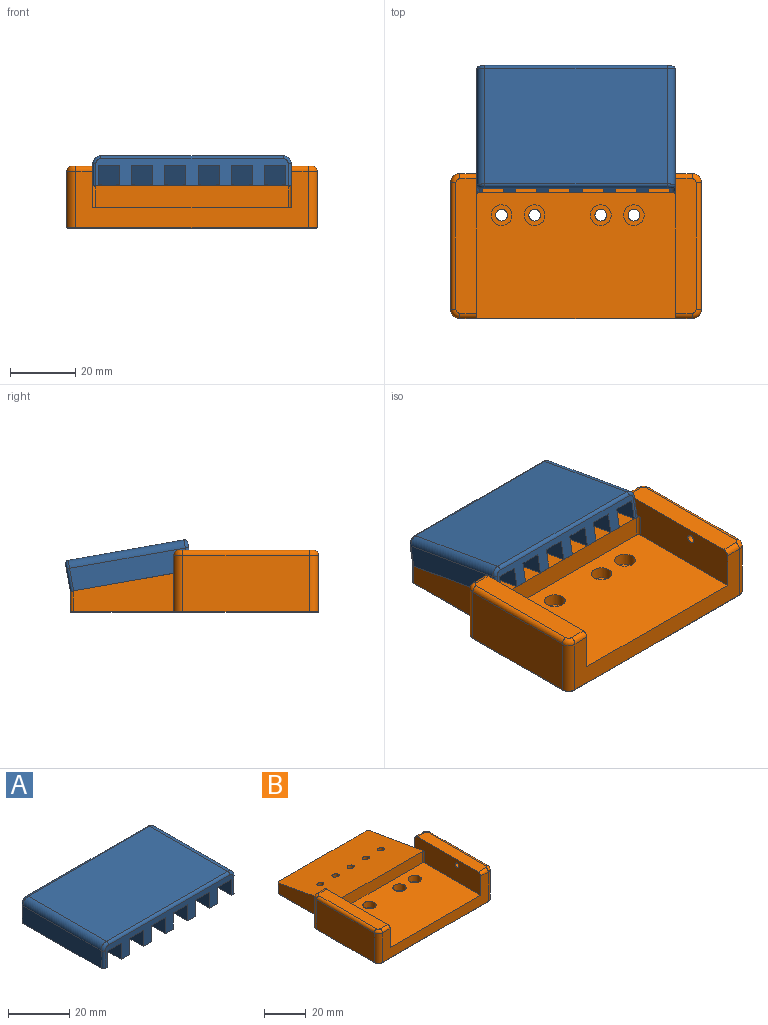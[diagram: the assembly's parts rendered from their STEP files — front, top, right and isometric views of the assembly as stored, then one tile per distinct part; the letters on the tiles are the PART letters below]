
ASSEMBLY  parts=2 mates=1
PART A: 58 faces, bbox 61.4x38.1x10.2 mm
  f0: plane 59.01x8.53mm, normal (0,-1,0), area 250.4mm2, adj f8,f9,f10,f11,f12,f13,f14,f17
  f1: plane 59.01x8.53mm, normal (0,1,0), area 439.9mm2, adj f23,f40,f41,f42,f43,f44,f45,f46
  f2: cylinder r=3.24mm len=6.48mm, axis (0,0,-1), area 55.1mm2, adj f13,f14,f23,f29,f45
  f3: cylinder r=3.24mm len=6.48mm, axis (0,0,-1), area 55.1mm2, adj f12,f21,f23,f24,f44
  f4: cylinder r=3.24mm len=6.48mm, axis (0,0,-1), area 55.1mm2, adj f11,f18,f23,f27,f43
  f5: cylinder r=3.24mm len=6.48mm, axis (0,0,-1), area 55.1mm2, adj f10,f17,f23,f28,f42
  f6: cylinder r=3.24mm len=6.48mm, axis (0,0,-1), area 55.1mm2, adj f9,f20,f23,f25,f41
  f7: cylinder r=3.24mm len=6.48mm, axis (0,0,-1), area 55.1mm2, adj f8,f19,f23,f26,f40
  f8: plane 32.32x6.48mm, normal (1,0,0), area 209.3mm2, adj f0,f7,f23,f26
  f9: plane 32.32x6.48mm, normal (1,0,0), area 209.3mm2, adj f0,f6,f23,f25
  f10: plane 32.32x6.48mm, normal (1,0,0), area 209.3mm2, adj f0,f5,f23,f28
  f11: plane 32.32x6.48mm, normal (1,0,0), area 209.3mm2, adj f0,f4,f23,f27
  f12: plane 32.32x6.48mm, normal (1,0,0), area 209.3mm2, adj f0,f3,f23,f24
  f13: plane 32.32x6.48mm, normal (1,0,0), area 209.3mm2, adj f0,f2,f23,f29
  f14: plane 32.32x6.48mm, normal (-1,0,0), area 209.3mm2, adj f0,f2,f23,f29
  f15: plane 36.1x7.03mm, normal (-1,0,0), area 253.6mm2, adj f23,f48,f51,f53
  f16: plane 36.1x7.03mm, normal (1,0,0), area 253.6mm2, adj f23,f46,f49,f56
  f17: plane 32.32x6.48mm, normal (-1,0,0), area 209.3mm2, adj f0,f5,f23,f28
  f18: plane 32.32x6.48mm, normal (-1,0,0), area 209.3mm2, adj f0,f4,f23,f27
  f19: plane 32.32x6.48mm, normal (-1,0,0), area 209.3mm2, adj f0,f7,f23,f26
  f20: plane 32.32x6.48mm, normal (-1,0,0), area 209.3mm2, adj f0,f6,f23,f25
  f21: plane 32.32x6.48mm, normal (-1,0,0), area 209.3mm2, adj f0,f3,f23,f24
  f22: plane 56.01x36.1mm, normal (0,0,1), area 2022mm2, adj f47,f50,f53,f56
  f23: plane 61.01x38.1mm, normal (0,0,-1), area 943.8mm2, adj f0,f1,f2,f3,f4,f5,f6,f7
  f24: plane 35.56x6.48mm, normal (0,0,-1), area 225.8mm2, adj f0,f3,f12,f21
  f25: plane 35.56x6.48mm, normal (0,0,-1), area 225.8mm2, adj f0,f6,f9,f20
  f26: plane 35.56x6.48mm, normal (0,0,-1), area 225.8mm2, adj f0,f7,f8,f19
  f27: plane 35.56x6.48mm, normal (0,0,-1), area 225.8mm2, adj f0,f4,f11,f18
  f28: plane 35.56x6.48mm, normal (0,0,-1), area 225.8mm2, adj f0,f5,f10,f17
  f29: plane 35.56x6.48mm, normal (0,0,-1), area 225.8mm2, adj f0,f2,f13,f14
  f30: cylinder r=1.25mm len=7.73mm, axis (0,0.17,-0.98), area 56.4mm2, adj f23,f31
  f31: cone r=0mm half-angle=59deg, axis (0,0.17,-0.98), area 5.7mm2, adj f30
  f32: cylinder r=1.25mm len=7.73mm, axis (0,0.17,-0.98), area 56.4mm2, adj f23,f33
  f33: cone r=0mm half-angle=59deg, axis (0,0.17,-0.98), area 5.7mm2, adj f32
  f34: cylinder r=1.25mm len=7.73mm, axis (0,0.17,-0.98), area 56.4mm2, adj f23,f35
  f35: cone r=0mm half-angle=59deg, axis (0,0.17,-0.98), area 5.7mm2, adj f34
  f36: cylinder r=1.25mm len=7.73mm, axis (0,0.17,-0.98), area 56.4mm2, adj f23,f37
  f37: cone r=0mm half-angle=59deg, axis (0,0.17,-0.98), area 5.7mm2, adj f36
  f38: cylinder r=1.25mm len=7.73mm, axis (0,0.17,-0.98), area 56.4mm2, adj f23,f39
  f39: cone r=0mm half-angle=59deg, axis (0,0.17,-0.98), area 5.7mm2, adj f38
  f40: cylinder r=1.82mm len=3.63mm, axis (0,-1,0), area 32.1mm2, adj f1,f7
  f41: cylinder r=1.82mm len=3.63mm, axis (0,-1,0), area 32.1mm2, adj f1,f6
  f42: cylinder r=1.82mm len=3.63mm, axis (0,-1,0), area 32.1mm2, adj f1,f5
  f43: cylinder r=1.82mm len=3.63mm, axis (0,-1,0), area 32.1mm2, adj f1,f4
  f44: cylinder r=1.82mm len=3.63mm, axis (0,-1,0), area 32.1mm2, adj f1,f3
  f45: cylinder r=1.82mm len=3.63mm, axis (0,-1,0), area 32.1mm2, adj f1,f2
  f46: cylinder r=1mm len=7.03mm, axis (0,0,-1), area 11mm2, adj f1,f16,f23,f57
  f47: cylinder r=1mm len=56.01mm, axis (1,0,0), area 88mm2, adj f1,f22,f54,f57
  f48: cylinder r=1mm len=7.03mm, axis (0,0,1), area 11mm2, adj f1,f15,f23,f54
  f49: cylinder r=1mm len=7.03mm, axis (0,0,1), area 11mm2, adj f0,f16,f23,f55
  f50: cylinder r=1mm len=56.01mm, axis (-1,0,0), area 88mm2, adj f0,f22,f52,f55
  f51: cylinder r=1mm len=7.03mm, axis (0,0,-1), area 11mm2, adj f0,f15,f23,f52
  f52: torus R=1.5mm, axis (0,-1,0), area 5.3mm2, adj f0,f50,f51,f53
  f53: cylinder r=2.5mm len=36.1mm, axis (0,1,0), area 141.8mm2, adj f15,f22,f52,f54
  f54: torus R=1.5mm, axis (0,-1,0), area 5.3mm2, adj f1,f47,f48,f53
  f55: torus R=1.5mm, axis (0,-1,0), area 5.3mm2, adj f0,f49,f50,f56
  f56: cylinder r=2.5mm len=36.1mm, axis (0,-1,0), area 141.8mm2, adj f16,f22,f55,f57
  f57: torus R=1.5mm, axis (0,-1,0), area 5.3mm2, adj f1,f46,f47,f56
PART B: 76 faces, bbox 77.5x76.6x19.2 mm
  f0: plane 44.45x12.7mm, normal (-1,0,0), area 518.2mm2, adj f3,f7,f9,f10,f30,f34,f40,f73
  f1: plane 44.45x12.7mm, normal (1,0,0), area 523.1mm2, adj f3,f7,f11,f13,f35,f39,f40,f74
  f2: plane 30.75x11.69mm, normal (-1,0,0), area 276.2mm2, adj f11,f40,f58,f62
  f3: plane 71.42x17.21mm, normal (0,-1,0), area 550mm2, adj f0,f1,f7,f26,f28,f30,f35,f65
  f4: plane 30.75x11.69mm, normal (1,0,0), area 276.2mm2, adj f9,f40,f57,f70
  f5: plane 59.11x6.1mm, normal (0,1,0), area 360.3mm2, adj f40,f57,f58,f66
  f6: plane 76.45x75.69mm, normal (0,0,-1), area 5071.3mm2, adj f14,f17,f20,f23,f44,f47,f50,f53
  f7: plane 61.11x38.68mm, normal (0,0,1), area 2236.8mm2, adj f0,f1,f3,f16,f19,f22,f25,f41
  f8: plane 38.91x17.21mm, normal (1,0,0), area 664.7mm2, adj f26,f27,f32,f69,f75
  f9: plane 17.21x5.16mm, normal (0,1,0), area 88.7mm2, adj f0,f4,f27,f34,f72
  f10: plane 41.28x6.34mm, normal (0,0,1), area 261mm2, adj f0,f30,f31,f32,f33,f34
  f11: plane 17.21x5.16mm, normal (0,1,0), area 88.7mm2, adj f1,f2,f29,f39,f60
  f12: plane 38.91x17.21mm, normal (-1,0,0), area 669.6mm2, adj f28,f29,f37,f61
  f13: plane 41.28x6.34mm, normal (0,0,1), area 261mm2, adj f1,f35,f36,f37,f38,f39
  f14: cylinder r=1.8mm len=3.61mm, axis (0,0,1), area 28.8mm2, adj f6,f15
  f15: plane 6.35x6.35mm, normal (0,0,1), area 21.5mm2, adj f14,f16
  f16: cylinder r=3.17mm len=6.35mm, axis (0,0,1), area 76mm2, adj f7,f15
  f17: cylinder r=1.8mm len=3.61mm, axis (0,0,1), area 28.8mm2, adj f6,f18
  f18: plane 6.35x6.35mm, normal (0,0,1), area 21.5mm2, adj f17,f19
  f19: cylinder r=3.17mm len=6.35mm, axis (0,0,1), area 76mm2, adj f7,f18
  f20: cylinder r=1.8mm len=3.61mm, axis (0,0,1), area 28.8mm2, adj f6,f21
  f21: plane 6.35x6.35mm, normal (0,0,1), area 21.5mm2, adj f20,f22
  f22: cylinder r=3.17mm len=6.35mm, axis (0,0,1), area 76mm2, adj f7,f21
  f23: cylinder r=1.8mm len=3.61mm, axis (0,0,1), area 28.8mm2, adj f6,f24
  f24: plane 6.35x6.35mm, normal (0,0,1), area 21.5mm2, adj f23,f25
  f25: cylinder r=3.17mm len=6.35mm, axis (0,0,1), area 76mm2, adj f7,f24
  f26: cylinder r=2.77mm len=17.21mm, axis (0,0,1), area 74.8mm2, adj f3,f8,f31,f67
  f27: cylinder r=2.77mm len=17.21mm, axis (0,0,1), area 74.8mm2, adj f8,f9,f33,f71
  f28: cylinder r=2.77mm len=17.21mm, axis (0,0,-1), area 74.8mm2, adj f3,f12,f36,f63
  f29: cylinder r=2.77mm len=17.21mm, axis (0,0,1), area 74.8mm2, adj f11,f12,f38,f59
  f30: cylinder r=1.59mm len=5.16mm, axis (1,0,0), area 12.9mm2, adj f0,f3,f10,f31
  f31: torus R=1.18mm, axis (0,0,1), area 8.6mm2, adj f10,f26,f30,f32
  f32: cylinder r=1.59mm len=38.91mm, axis (0,-1,0), area 97mm2, adj f8,f10,f31,f33
  f33: torus R=1.18mm, axis (0,0,1), area 8.6mm2, adj f10,f27,f32,f34
  f34: cylinder r=1.59mm len=5.16mm, axis (1,0,0), area 12.9mm2, adj f0,f9,f10,f33
  f35: cylinder r=1.59mm len=5.16mm, axis (-1,0,0), area 12.9mm2, adj f1,f3,f13,f36
  f36: torus R=1.18mm, axis (0,0,1), area 8.6mm2, adj f13,f28,f35,f37
  f37: cylinder r=1.59mm len=38.91mm, axis (0,1,0), area 97mm2, adj f12,f13,f36,f38
  f38: torus R=1.18mm, axis (0,0,1), area 8.6mm2, adj f13,f29,f37,f39
  f39: cylinder r=1.59mm len=5.16mm, axis (1,0,0), area 12.9mm2, adj f1,f11,f13,f38
  f40: plane 61.24x38.41mm, normal (0,0.17,0.98), area 2282.1mm2, adj f0,f1,f2,f4,f5,f41,f42,f45
  f41: plane 59.59x6.62mm, normal (0,-1,0), area 394.2mm2, adj f7,f40,f73,f74
  f42: cylinder r=1.7mm len=6.2mm, axis (0,0,-1), area 63.1mm2, adj f40,f43
  f43: plane 6.5x6.5mm, normal (0,0,-1), area 24.1mm2, adj f42,f44
  f44: cylinder r=3.25mm len=6.5mm, axis (0,0,-1), area 77.8mm2, adj f6,f43
  f45: cylinder r=1.7mm len=6.2mm, axis (0,0,-1), area 63.1mm2, adj f40,f46
  f46: plane 6.5x6.5mm, normal (0,0,-1), area 24.1mm2, adj f45,f47
  f47: cylinder r=3.25mm len=6.5mm, axis (0,0,-1), area 77.8mm2, adj f6,f46
  f48: cylinder r=1.7mm len=6.2mm, axis (0,0,-1), area 63.1mm2, adj f40,f49
  f49: plane 6.5x6.5mm, normal (0,0,-1), area 24.1mm2, adj f48,f50
  f50: cylinder r=3.25mm len=6.5mm, axis (0,0,-1), area 77.8mm2, adj f6,f49
  f51: cylinder r=1.7mm len=6.2mm, axis (0,0,-1), area 63.1mm2, adj f40,f52
  f52: plane 6.5x6.5mm, normal (0,0,-1), area 24.1mm2, adj f51,f53
  f53: cylinder r=3.25mm len=6.5mm, axis (0,0,-1), area 77.8mm2, adj f6,f52
  f54: cylinder r=1.7mm len=6.2mm, axis (0,0,-1), area 63.1mm2, adj f40,f55
  f55: plane 6.5x6.5mm, normal (0,0,-1), area 24.1mm2, adj f54,f56
  f56: cylinder r=3.25mm len=6.5mm, axis (0,0,-1), area 77.8mm2, adj f6,f55
  f57: cylinder r=1mm len=6.27mm, axis (0,0,-1), area 9.7mm2, adj f4,f5,f40,f68
  f58: cylinder r=1mm len=6.27mm, axis (0,0,1), area 9.7mm2, adj f2,f5,f40,f64
  f59: torus R=2.51mm, axis (0,0,1), area 1.7mm2, adj f6,f29,f60,f61
  f60: cylinder r=0.25mm len=5.41mm, axis (-1,0,0), area 2.1mm2, adj f6,f11,f59,f62
  f61: cylinder r=0.25mm len=38.91mm, axis (0,-1,0), area 15.5mm2, adj f6,f12,f59,f63
  f62: cylinder r=0.25mm len=31mm, axis (0,-1,0), area 12.3mm2, adj f2,f6,f60,f64
  f63: torus R=2.51mm, axis (0,0,1), area 1.7mm2, adj f6,f28,f61,f65
  f64: torus R=0.75mm, axis (0,0,1), area 0.6mm2, adj f6,f58,f62,f66
  f65: cylinder r=0.25mm len=71.42mm, axis (1,0,0), area 28.5mm2, adj f3,f6,f63,f67
  f66: cylinder r=0.25mm len=59.11mm, axis (-1,0,0), area 23.6mm2, adj f5,f6,f64,f68
  f67: torus R=2.51mm, axis (0,0,1), area 1.7mm2, adj f6,f26,f65,f69
  f68: torus R=0.75mm, axis (0,0,1), area 0.6mm2, adj f6,f57,f66,f70
  f69: cylinder r=0.25mm len=38.91mm, axis (0,1,0), area 15.5mm2, adj f6,f8,f67,f71
  f70: cylinder r=0.25mm len=31mm, axis (0,1,0), area 12.3mm2, adj f4,f6,f68,f72
  f71: torus R=2.51mm, axis (0,0,1), area 1.7mm2, adj f6,f27,f69,f72
  f72: cylinder r=0.25mm len=5.41mm, axis (-1,0,0), area 2.1mm2, adj f6,f9,f70,f71
  f73: cylinder r=0.76mm len=6.75mm, axis (0,0,1), area 8mm2, adj f0,f7,f40,f41
  f74: cylinder r=0.76mm len=6.75mm, axis (0,0,-1), area 8mm2, adj f1,f7,f40,f41
  f75: cylinder r=1.25mm len=7.93mm, axis (1,0,0), area 62.2mm2, adj f0,f8
PLACE A rot(axis=(-1,0,0),10deg) t=(0,19.34,9.66)mm
PLACE B at identity
MATE fastened A.f23 <-> B.f40  axis (0,0.17,0.98) through (0,19.05,9.71)mm
